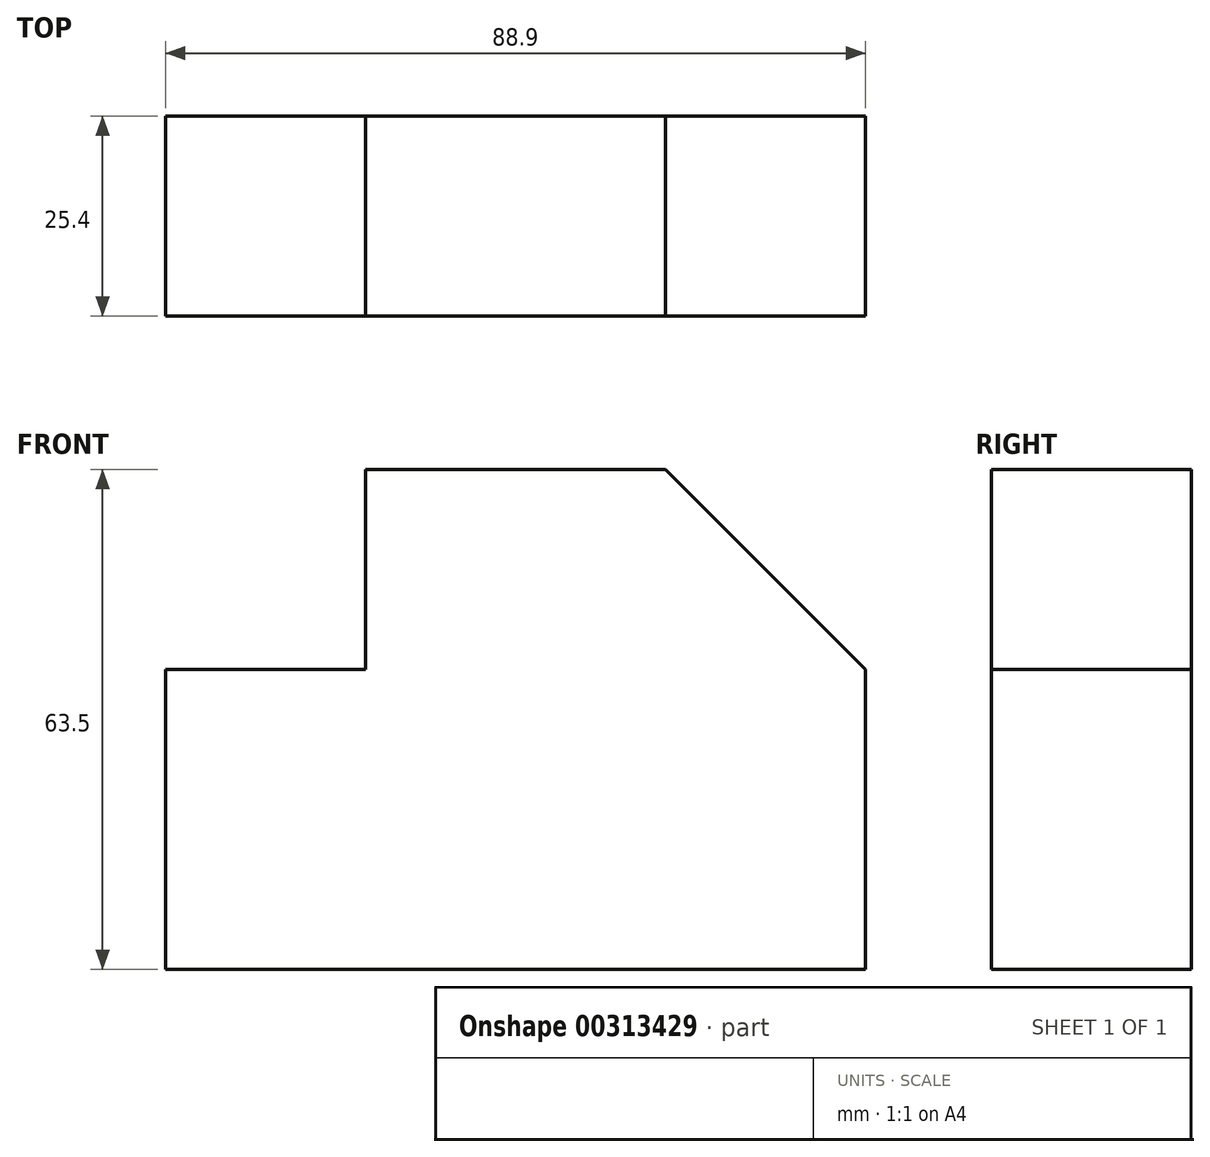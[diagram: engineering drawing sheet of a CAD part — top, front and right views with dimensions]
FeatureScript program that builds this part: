
annotation { "Feature Type Name" : "Feature", "Feature Type Description" : "" }
export const myFeature = defineFeature(function(context is Context, id is Id, definition is map)
    precondition{}
    {
        {
            var Q0;
            Q0=qCreatedBy(makeId("Front.planeOp"),FACE);
            var sketch = newSketch(context, id + "F0", { "sketchPlane" : qUnion([Q0])});
            skLineSegment(sketch, "E0", {"start": v(-52.2, -25.81) * mm, "end": v(36.7, -25.81) * mm});
            skLineSegment(sketch, "E1", {"start": v(-52.2, -25.81) * mm, "end": v(-52.2, 12.29) * mm});
            skLineSegment(sketch, "E2", {"start": v(-52.2, 12.29) * mm, "end": v(-26.8, 12.29) * mm});
            skLineSegment(sketch, "E3", {"start": v(-26.8, 12.29) * mm, "end": v(-26.8, 37.69) * mm});
            skLineSegment(sketch, "E4", {"start": v(-26.8, 37.69) * mm, "end": v(11.3, 37.69) * mm});
            skLineSegment(sketch, "E5", {"start": v(11.3, 37.69) * mm, "end": v(36.7, 12.29) * mm});
            skLineSegment(sketch, "E6", {"start": v(36.7, 12.29) * mm, "end": v(36.7, -25.81) * mm});
            skSolve(sketch);
        }
        {
            var Q0;
            Q0=makeQuery(id+"F0.imprint","IMPRINT",FACE,{"disambiguationData":[TD([[makeQuery(id+"F0.imprint","IMPRINT",EDGE,{"derivedFrom":sQuery(id+"F0.wireOp",EDGE,"E0")}),1.0]])]});
            extrude(context, id + "F1", {"entities" : qUnion([Q0]), "depth" : 25.4 * mm});
        }
    });
